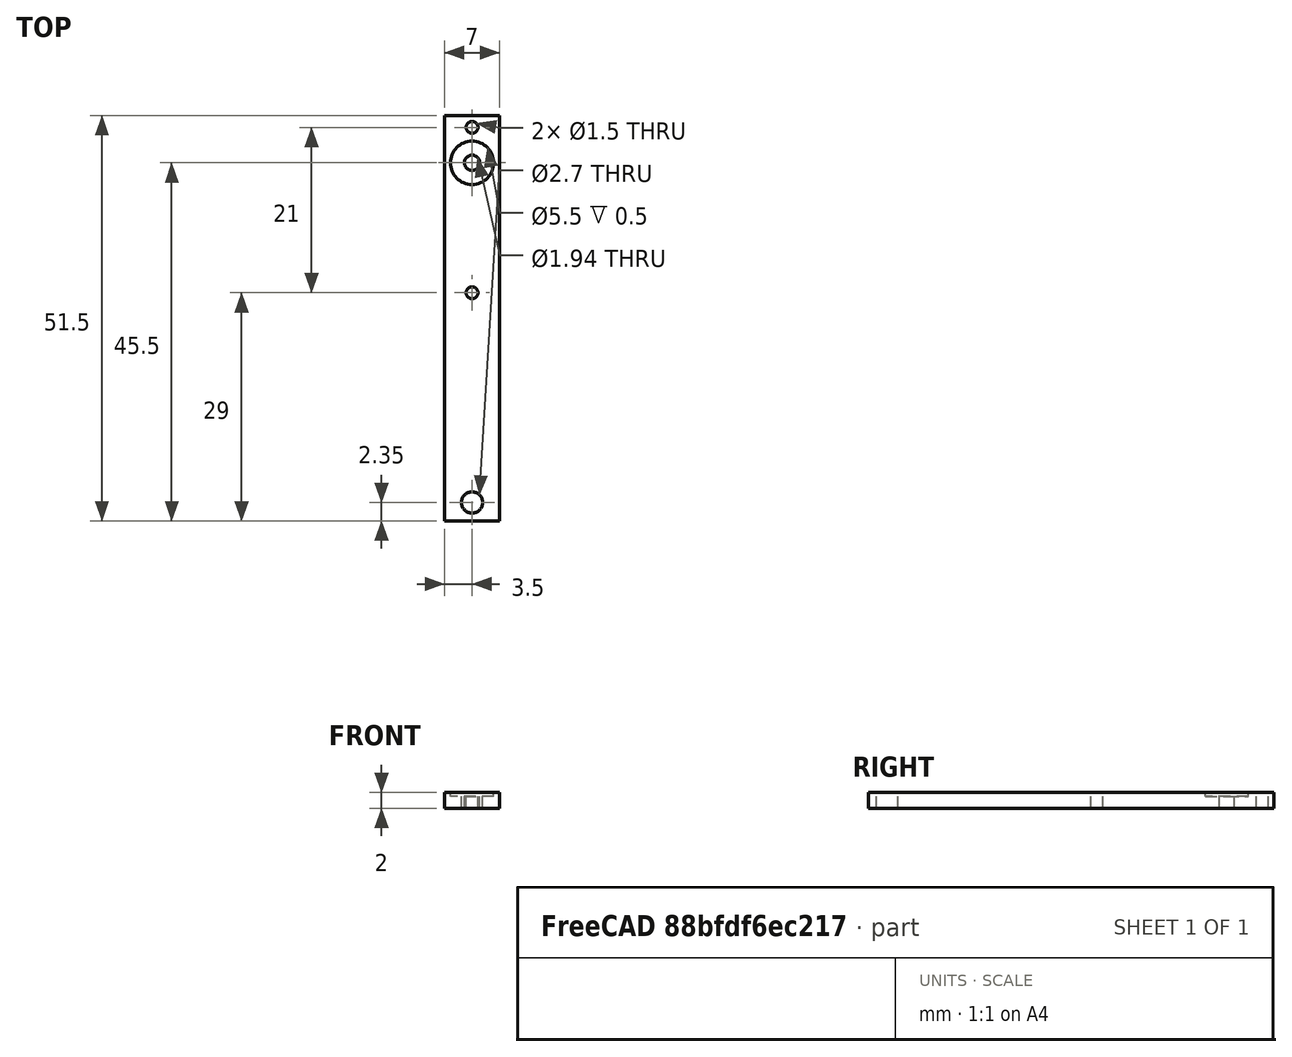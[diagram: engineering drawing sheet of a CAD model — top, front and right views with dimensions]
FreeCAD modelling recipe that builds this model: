
FCSTD DOCUMENT
Label: servoArm
objects: Part::Cylinder×5, Part::Cut×5, Part::Box×1
note: 11 computed .brp shape members not serialized (recipe doc carries the construction recipe); baked Part::Feature solids carry a one-line shape summary decoded from their .brp

FEATURE [Part::Box] Box
  Height = 2
  Length = 7
  Width = 51.5
FEATURE [Part::Cylinder] Cylinder
  Angle = 360
  Height = 0.5
  Placement = pos=(3.5,45.5,1.5) rot=(0,0,1;0rad)
  Radius = 2.75
FEATURE [Part::Cut] Cut
  Base = -> Box
  Tool = -> Cylinder
FEATURE [Part::Cylinder] Cylinder001
  Angle = 360
  Height = 2
  Placement = pos=(3.5,45.5,0) rot=(0,0,1;0rad)
  Radius = 0.97
FEATURE [Part::Cut] Cut001
  Base = -> Cut
  Tool = -> Cylinder001
FEATURE [Part::Cylinder] Cylinder002
  Angle = 360
  Height = 2
  Placement = pos=(3.5,50,0) rot=(0,0,1;0rad)
  Radius = 0.75
FEATURE [Part::Cylinder] Cylinder003
  Angle = 360
  Height = 2
  Placement = pos=(3.5,29,0) rot=(0,0,1;0rad)
  Radius = 0.75
FEATURE [Part::Cut] Cut002
  Base = -> Cut001
  Tool = -> Cylinder002
FEATURE [Part::Cut] Cut003
  Base = -> Cut002
  Tool = -> Cylinder003
FEATURE [Part::Cylinder] Cylinder004
  Angle = 360
  Height = 2
  Placement = pos=(3.5,2.35,0) rot=(0,0,1;0rad)
  Radius = 1.35
FEATURE [Part::Cut] Cut004
  Base = -> Cut003
  Tool = -> Cylinder004
